# Revit family: leddownlightrc-b_rd150-12w-3000-wh_540001023800
name_source: partatom
category: Leuchten
revit_build: Autodesk Revit 2016 (Build: 20190508_0715(x64)
units: mm (PartAtom-declared; Revit-internal decimal feet)

## family parameters
Basisbauteil = Fläche
Beim Laden mit Abzugskörper schneiden = Nein
Bemaßung runder Anschluss = Durchmesser verwenden
Gemeinsam genutzt = Nein
Lichtquelle = Nein
Raumberechnungspunkt = Nein
Teiletyp = Normal

## types (1)
- LEDDownlightRc-B Rd150-12W-3000-WH (1 x LED, 900 lm)
    Approval mark = CE
    Beschreibung = Suitable for recessed applications. Energy saving up to 60%. Flicker-free light with perfect uniformity. Easy to install due to integrated LED driver.
    CIE Flux Codes = 47 78 95 99 100
    Control Gear = Electronic ballast
    Height = 0 mm  [stored 0 ft]
    Hersteller = OPPLE
    Lamp Light Flux = 900 lm
    Lamp count = 1
    Lampe = 1 x LED
    Length = 162 mm
    Luminous efficacy = 75 lm/W
    ModVariant = Nein
    Modell = 540001023800
    Mounting Place = Ceiling
    Mounting Type = Recessed
    Number of Poles = 1
    OnlyDefault = Ja
    Power Factor = 1
    Product Name = LEDDownlightRc-B Rd150-12W-3000-WH
    Product group = Downlight Basic
    ProductGroupID = 401
    Protection Class = Protection class II
    Protection Degree = IP 20
    RLX_Detail_Level = 1
    RlxData = <blob elided: 15701 chars, md5=21351b82>
    Scheinlast = 12 VA
    Socket = socket
    Standby Power = 0 W
    System Light Flux = 900 lm
    System Power = 12 W
    Typenbild = 540001023800.jpg
    Typenkommentare = Product without accessories
    URL = http://relux.com
    VarID = ---
    Voltage = 0 V
    Vorgabe-Ansicht = 1800 mm
    Weight = 0.00 kg
    Width = 0 mm  [stored 0 ft]

note: [stored X ft] marks values corroborated as IEEE doubles in the binary element streams (Revit-internal decimal feet)

## geometry (parser evidence)
native form markers: Blend x4, Sweep x13
no freeform markers — native parametric forms only
